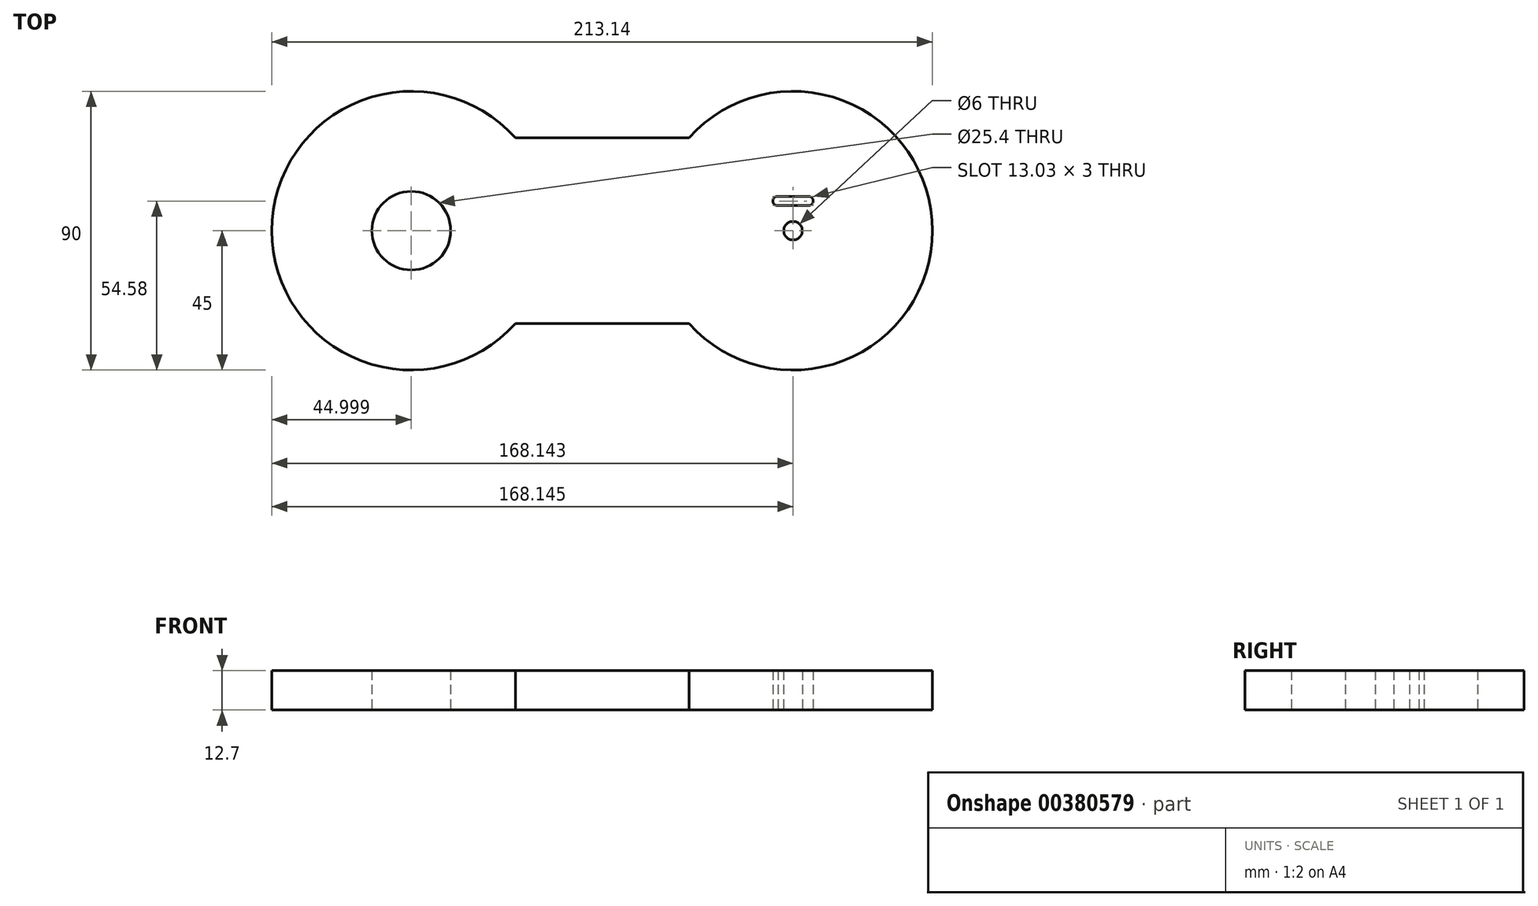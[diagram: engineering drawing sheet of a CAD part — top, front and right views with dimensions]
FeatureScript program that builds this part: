
annotation { "Feature Type Name" : "Feature", "Feature Type Description" : "" }
export const myFeature = defineFeature(function(context is Context, id is Id, definition is map)
    precondition{}
    {
        {
            var Q0;
            Q0=qCreatedBy(makeId("Top.planeOp"),FACE);
            var sketch = newSketch(context, id + "F0", { "sketchPlane" : qUnion([Q0])});
            skCircle(sketch, "E0", {"center": v(89.6, 0) * mm, "radius": 3 * mm});
            skCircle(sketch, "E1", {"center": v(89.6, 0) * mm, "radius": 45 * mm});
            skCircle(sketch, "E2", {"center": v(-33.54, 0) * mm, "radius": 45 * mm});
            skCircle(sketch, "E3", {"center": v(84.58, 9.58) * mm, "radius": 1.5 * mm});
            skCircle(sketch, "E4", {"center": v(94.62, 9.58) * mm, "radius": 1.5 * mm});
            skLineSegment(sketch, "E5", {"start": v(84.37, 11.07) * mm, "end": v(94.62, 11.08) * mm});
            skLineSegment(sketch, "E6", {"start": v(94.62, 8.08) * mm, "end": v(84.58, 8.08) * mm});
            skCircle(sketch, "E7", {"center": v(-33.54, 0) * mm, "radius": 12.7 * mm});
            skLineSegment(sketch, "E8", {"start": v(0, 30) * mm, "end": v(56.06, 30) * mm});
            skLineSegment(sketch, "E9", {"start": v(0, -30) * mm, "end": v(56.06, -30) * mm});
            skSolve(sketch);
        }
        {
            var Q0;
            Q0=makeQuery(id+"F0.imprint","IMPRINT",FACE,{"disambiguationData":[TD([[makeQuery(id+"F0.imprint","IMPRINT",EDGE,{"derivedFrom":sQuery(id+"F0.wireOp",EDGE,"E0")}),-1.0]])]});
            var Q1;
            {var subQ0=sQuery(id+"F0.wireOp",EDGE,"1c07OCq6-OmA0-Zw1x-DlE6-Oze77SioVY76");Q1=makeQuery(id+"F0.imprint","IMPRINT",FACE,{"disambiguationData":[TD([[makeQuery(id+"F0.imprint","IMPRINT",EDGE,{"derivedFrom":subQ0}),-1.0]])]});}
            var Q2;
            {var subQ0=sQuery(id+"F0.wireOp",EDGE,"E2");var subQ1=makeQuery(id+"F0.imprint","INTERSECT",VERTEX,{"derivedFrom":[subQ0,sQuery(id+"F0.wireOp",EDGE,"1c07OCq6-OmA0-Zw1x-DlE6-Oze77SioVY76")]});Q2=makeQuery(id+"F0.imprint","IMPRINT",FACE,{"disambiguationData":[TD([[makeQuery(id+"F0.imprint","IMPRINT",EDGE,{"disambiguationData":[TD([[subQ1,-1.0]])],"derivedFrom":subQ0}),1.0]])]});}
            var Q3;
            {var subQ0=sQuery(id+"F0.wireOp",EDGE,"E8");Q3=makeQuery(id+"F0.imprint","IMPRINT",FACE,{"disambiguationData":[TD([[makeQuery(id+"F0.imprint","IMPRINT",EDGE,{"derivedFrom":subQ0}),-1.0]])]});}
            extrude(context, id + "F1", {"entities" : qUnion([Q0, Q1, Q2, Q3]), "depth" : 12.7 * mm});
        }
    });
